# Revit family: VIESSMANN - Vitocell 100-W CUG CUGA CUGA-A 120-150 L
name_source: partatom
category: Wyposażenie mechaniczne
revit_build: Autodesk Revit 2017 (Build: 20160720_1515(x64)
units: mm (PartAtom-declared; Revit-internal decimal feet)

## family parameters
Numer OmniClass = 23.65.35.11.11
Oparty na płaszczyźnie roboczej = Nie
Punkt obliczania pomieszczeń = Nie
Tnij formami wycięć po wczytaniu = Nie
Typ części = Normalny
Tytuł OmniClass = Storage Water Heaters
Współdzielony = Nie
Wymiar okrągłego złącza = Użyj średnicy
Zawsze pionowo = Tak

## types (4) — shared parameters
Autor = https://www.archispace.pl
Ciepła woda użytkowa = 3/4"
Cyrkulacja = 3/4"
Dop. ciśnienie robocze po stronie wody grzewczej = 1000.000 kPa
Dop. ciśnienie robocze po stronie wody użytkowej = 1000.000 kPa
Dop. temperatura po stronie cwu = 95 °C
Dop. temperatura po stronie wody grzewczej = 160 °C
Numer identyfikacyjny produktu = 9W245/11-13MC/E
Opis = Podgrzewacz pojemnościowy
Opis indeksowy = 9W245/11-13MC/E
Powierzchnia grzewcza = 1.0 m²
Powrót wody grzewczej = 1"
Producent = Viessmann Sp.z.o.o.
URL = https://www.viessmann-projektant.pl
Viessmann Kolor 1 = Viessmann Kolor 1
Viessmann Kolor 2 = Viessmann Kolor 2
Viessmann Kolor 3 = Viessmann Kolor 3
Zasilanie wody grzewczej = 1"
Zimna woda użytkowa = 3/4"

## per-type parameters (varying)
| type | Długość | Ilość ciepła dyżurnego | Klasa efektywności energetycznej | Linia modelu | Masa całkowita | Model | Pojemność podgrzewacza | Wysokość | Średnica |
| Zbiornik CUGA 150L | 641 mm  [stored 2.10302 ft] | 1.21 kWh/24h | B | 711 mm | 88.00 kg | Podgrzewacz pojemnościowy Viessmann Vitocell 100-W CUGA 150L / Hot water storage tank Viessmann Vitocell 100-W CUGA 150L | 150.0 L | 942 mm  [stored 3.09055 ft] | 641 mm  [stored 2.10302 ft] |
| Zbiornik CUGA 120L | 596 mm  [stored 1.95538 ft] | 1.10 kWh/24h | B | 666 mm  [stored 2.18504 ft] | 75.00 kg | Podgrzewacz pojemnościowy Viessmann Vitocell 100-W CUGA 120L / Hot water storage tank Viessmann Vitocell 100-W CUGA 120L | 120.0 L | 914 mm  [stored 2.99869 ft] | 596 mm  [stored 1.95538 ft] |
| Zbiornik CUGA-A 120L | 596 mm  [stored 1.95538 ft] | 0.75 kWh/24h | A | 666 mm  [stored 2.18504 ft] | 75.00 kg | Podgrzewacz pojemnościowy Viessmann Vitocell 100-W CUGA-A 120L / Hot water storage tank Viessmann Vitocell 100-W CUGA-A 120L | 120.0 L | 914 mm  [stored 2.99869 ft] | 596 mm  [stored 1.95538 ft] |
| Zbiornik CUGA-A 150L | 641 mm  [stored 2.10302 ft] | 0.84 kWh/24h | A | 711 mm | 88.00 kg | Podgrzewacz pojemnościowy Viessmann Vitocell 100-W CUGA-A 150L / Hot water storage tank Viessmann Vitocell 100-W CUGA-A 150L | 150.0 L | 942 mm  [stored 3.09055 ft] | 641 mm  [stored 2.10302 ft] |

note: [stored X ft] marks values corroborated as IEEE doubles in the binary element streams (Revit-internal decimal feet)
